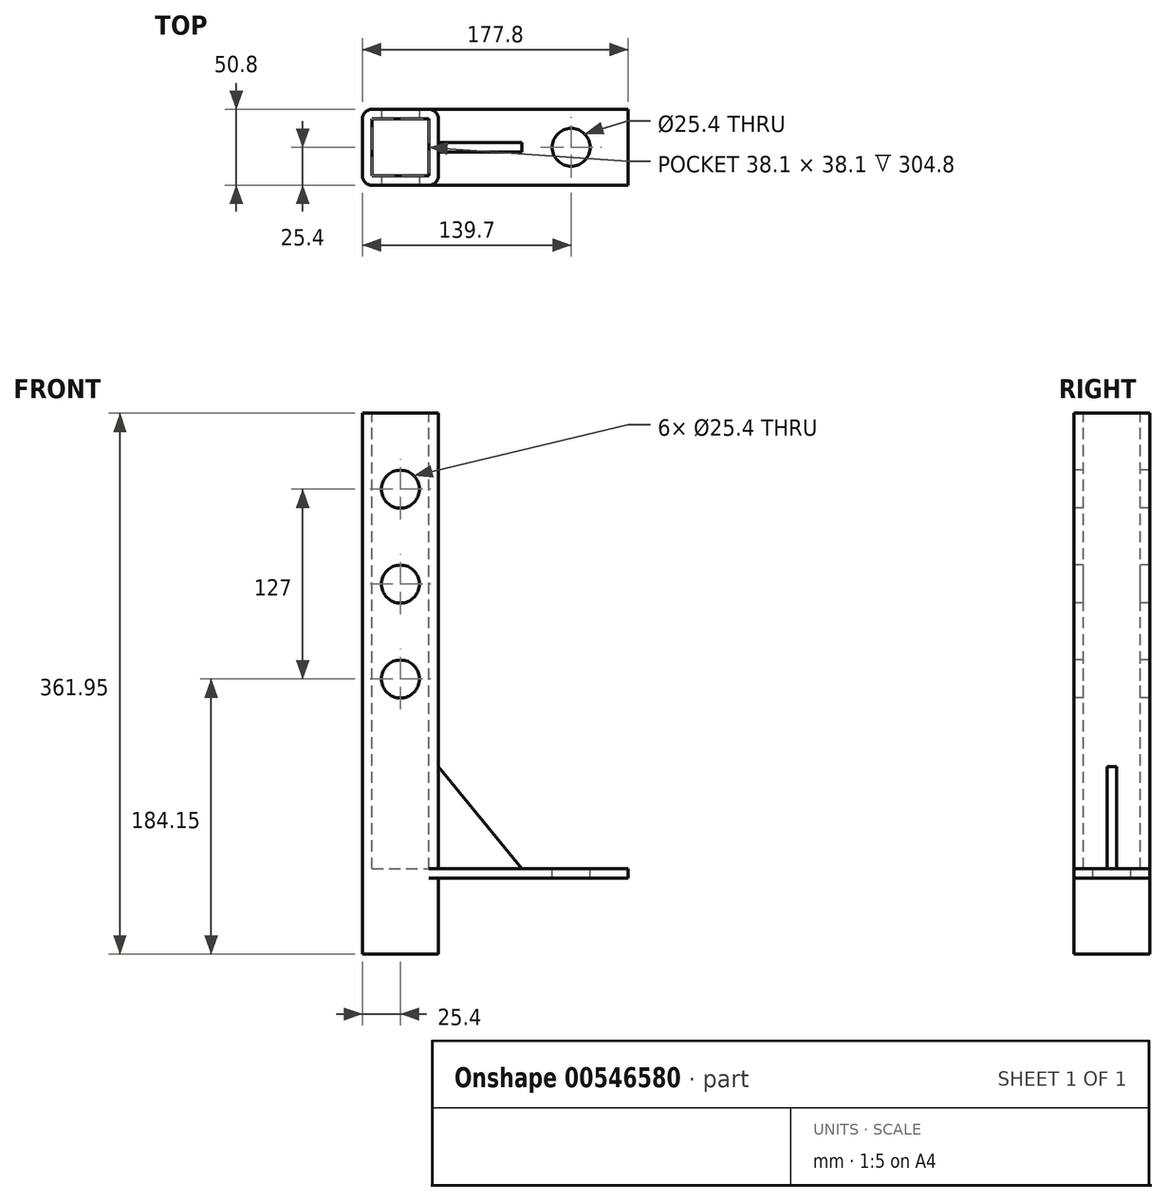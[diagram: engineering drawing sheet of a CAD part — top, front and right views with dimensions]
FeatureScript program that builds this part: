
annotation { "Feature Type Name" : "Feature", "Feature Type Description" : "" }
export const myFeature = defineFeature(function(context is Context, id is Id, definition is map)
    precondition{}
    {
        {
            var Q0;
            Q0=qCreatedBy(makeId("Top.planeOp"),FACE);
            var sketch = newSketch(context, id + "F0", { "sketchPlane" : qUnion([Q0])});
            skLineSegment(sketch, "E0.bottom", {"start": v(6.35, 0) * mm, "end": v(44.45, 0) * mm});
            skLineSegment(sketch, "E0.top", {"start": v(6.35, 50.8) * mm, "end": v(44.45, 50.8) * mm});
            skLineSegment(sketch, "E0.left", {"start": v(0, 6.35) * mm, "end": v(0, 44.45) * mm});
            skLineSegment(sketch, "E0.right", {"start": v(50.8, 6.35) * mm, "end": v(50.8, 44.45) * mm});
            skPoint(sketch, "E1.visualSharp", {"position": v(0, 50.8) * mm});
            skArc(sketch, "E1.filletArc", {"start": v(6.35, 50.8) * mm, "mid": v(1.86, 48.94) * mm, "end": v(0, 44.45) * mm});
            skPoint(sketch, "E2.visualSharp", {"position": v(50.8, 50.8) * mm});
            skArc(sketch, "E2.filletArc", {"start": v(50.8, 44.45) * mm, "mid": v(48.94, 48.94) * mm, "end": v(44.45, 50.8) * mm});
            skPoint(sketch, "E3.visualSharp", {"position": v(50.8, 0) * mm});
            skArc(sketch, "E3.filletArc", {"start": v(44.45, 0) * mm, "mid": v(48.94, 1.86) * mm, "end": v(50.8, 6.35) * mm});
            skPoint(sketch, "E4.visualSharp", {"position": v(0, 0) * mm});
            skArc(sketch, "E4.filletArc", {"start": v(0, 6.35) * mm, "mid": v(1.86, 1.86) * mm, "end": v(6.35, 0) * mm});
            skLineSegment(sketch, "E5.0", {"start": v(6.35, 44.45) * mm, "end": v(44.45, 44.45) * mm});
            skLineSegment(sketch, "E5.1", {"start": v(6.35, 6.35) * mm, "end": v(6.35, 44.45) * mm});
            skLineSegment(sketch, "E5.2", {"start": v(6.35, 6.35) * mm, "end": v(44.45, 6.35) * mm});
            skLineSegment(sketch, "E5.3", {"start": v(44.45, 6.35) * mm, "end": v(44.45, 44.45) * mm});
            skSolve(sketch);
        }
        {
            var Q0;
            Q0=makeQuery(id+"F0.imprint","IMPRINT",FACE,{"disambiguationData":[TD([[makeQuery(id+"F0.imprint","IMPRINT",EDGE,{"derivedFrom":sQuery(id+"F0.wireOp",EDGE,"E0.bottom")}),1.0]])]});
            extrude(context, id + "F1", {"entities" : qUnion([Q0]), "oppositeDirection" : true, "depth" : 304.8 * mm, "offsetDistance" : 25.4 * mm, "symmetric" : true});
        }
        {
            var Q0;
            Q0=makeQuery(id+"F1.opExtrude","SWEPT_FACE",FACE,{"disambiguationData":[OSD([sQuery(id+"F0.wireOp",EDGE,"E0.bottom")])]});
            var sketch = newSketch(context, id + "F2", { "sketchPlane" : qUnion([Q0])});
            skCircle(sketch, "E6", {"center": v(25.4, 101.6) * mm, "radius": 12.7 * mm});
            skCircle(sketch, "E7", {"center": v(25.4, 38.1) * mm, "radius": 12.7 * mm});
            skCircle(sketch, "E8", {"center": v(25.4, -25.4) * mm, "radius": 12.7 * mm});
            skLineSegment(sketch, "E9", {"start": v(25.4, 152.4) * mm, "end": v(25.4, -152.4) * mm, "construction": true});
            skSolve(sketch);
        }
        {
            var Q0;
            Q0 = qSketchRegion(id + "F2", true);
            extrude(context, id + "F3", {"entities" : qUnion([Q0]), "operationType" : NewBodyOperationType.REMOVE, "endBound" : BoundingType.THROUGH_ALL, "oppositeDirection" : true, "depth" : 25.4 * mm, "offsetDistance" : 25.4 * mm});
        }
        {
            var Q0;
            Q0=makeQuery(id+"F1.opExtrude","CAP_FACE",FACE,{"disambiguationData":[OSD([sQuery(id+"F0.wireOp",EDGE,"E0.bottom"),sQuery(id+"F0.wireOp",EDGE,"E0.top"),sQuery(id+"F0.wireOp",EDGE,"E0.left"),sQuery(id+"F0.wireOp",EDGE,"E0.right"),sQuery(id+"F0.wireOp",EDGE,"E1.filletArc"),sQuery(id+"F0.wireOp",EDGE,"E2.filletArc"),sQuery(id+"F0.wireOp",EDGE,"E3.filletArc"),sQuery(id+"F0.wireOp",EDGE,"E4.filletArc"),sQuery(id+"F0.wireOp",EDGE,"E5.0"),sQuery(id+"F0.wireOp",EDGE,"E5.1"),sQuery(id+"F0.wireOp",EDGE,"E5.2"),sQuery(id+"F0.wireOp",EDGE,"E5.3")])],"isStart":false});
            var sketch = newSketch(context, id + "F4", { "sketchPlane" : qUnion([Q0])});
            skLineSegment(sketch, "E10.0", {"start": v(0, -6.35) * mm, "end": v(0, -44.45) * mm});
            skArc(sketch, "E11.0", {"start": v(6.35, -50.8) * mm, "mid": v(1.86, -48.94) * mm, "end": v(0, -44.45) * mm});
            skLineSegment(sketch, "E12.0", {"start": v(6.35, -50.8) * mm, "end": v(44.45, -50.8) * mm});
            skLineSegment(sketch, "E13.0", {"start": v(50.8, -6.35) * mm, "end": v(50.8, -44.45) * mm});
            skArc(sketch, "E14.0", {"start": v(50.8, -44.45) * mm, "mid": v(48.94, -48.94) * mm, "end": v(44.45, -50.8) * mm});
            skArc(sketch, "E15.0", {"start": v(44.45, 0) * mm, "mid": v(48.94, -1.86) * mm, "end": v(50.8, -6.35) * mm});
            skLineSegment(sketch, "E16.0", {"start": v(6.35, 0) * mm, "end": v(44.45, 0) * mm});
            skArc(sketch, "E17.0", {"start": v(0, -6.35) * mm, "mid": v(1.86, -1.86) * mm, "end": v(6.35, 0) * mm});
            skPoint(sketch, "E18.0", {"position": v(0, 0) * mm});
            skLineSegment(sketch, "E19.bottom", {"start": v(6.35, 0) * mm, "end": v(177.8, 0) * mm});
            skLineSegment(sketch, "E19.top", {"start": v(6.35, -50.8) * mm, "end": v(177.8, -50.8) * mm});
            skLineSegment(sketch, "E19.right", {"start": v(177.8, 0) * mm, "end": v(177.8, -50.8) * mm});
            skArc(sketch, "E20.filletArc", {"start": v(6.35, 0) * mm, "mid": v(1.86, -1.86) * mm, "end": v(0, -6.35) * mm});
            skPoint(sketch, "E21.visualSharp", {"position": v(0, -50.8) * mm});
            skArc(sketch, "E21.filletArc", {"start": v(0, -44.45) * mm, "mid": v(1.86, -48.94) * mm, "end": v(6.35, -50.8) * mm});
            skSolve(sketch);
        }
        {
            var Q0;
            Q0 = qSketchRegion(id + "F4", true);
            extrude(context, id + "F5", {"entities" : qUnion([Q0]), "operationType" : NewBodyOperationType.ADD, "depth" : 6.35 * mm, "offsetDistance" : 25.4 * mm});
        }
        {
            var Q0;
            {var subQ0=sQuery(id+"F4.wireOp",EDGE,"E19.bottom");var subQ1=sQuery(id+"F4.wireOp",EDGE,"E19.top");var subQ2=sQuery(id+"F4.wireOp",EDGE,"E19.right");Q0=makeQuery(id+"F5.boolean.opBoolean","SPLIT",FACE,{"disambiguationData":[TD([makeQuery(id+"F1.opExtrude","SWEPT_FACE",FACE,{"disambiguationData":[OSD([sQuery(id+"F0.wireOp",EDGE,"E0.bottom")])]})])],"derivedFrom":makeQuery(id+"F5.opExtrude","CAP_FACE",FACE,{"disambiguationData":[OSD([subQ0,subQ1,sQuery(id+"F4.wireOp",EDGE,"E10.0"),subQ2,sQuery(id+"F4.wireOp",EDGE,"E20.filletArc"),sQuery(id+"F4.wireOp",EDGE,"E21.filletArc")])],"isStart":true})});}
            var sketch = newSketch(context, id + "F6", { "sketchPlane" : qUnion([Q0])});
            skCircle(sketch, "E22", {"center": v(139.7, 25.4) * mm, "radius": 12.7 * mm});
            skLineSegment(sketch, "E23", {"start": v(177.8, 25.4) * mm, "end": v(50.8, 25.4) * mm, "construction": true});
            skSolve(sketch);
        }
        {
            var Q0;
            Q0 = qSketchRegion(id + "F6", true);
            extrude(context, id + "F7", {"entities" : qUnion([Q0]), "operationType" : NewBodyOperationType.REMOVE, "endBound" : BoundingType.THROUGH_ALL, "oppositeDirection" : true, "depth" : 25.4 * mm, "offsetDistance" : 25.4 * mm});
        }
        {
            var Q0;
            Q0=makeQuery(id+"F5.boolean.opBoolean","MERGE",FACE,{"derivedFrom":[makeQuery(id+"F1.opExtrude","SWEPT_FACE",FACE,{"disambiguationData":[OSD([sQuery(id+"F0.wireOp",EDGE,"E0.bottom")])]}),makeQuery(id+"F5.opExtrude","SWEPT_FACE",FACE,{"disambiguationData":[OSD([sQuery(id+"F4.wireOp",EDGE,"E19.bottom")])]})]});
            cPlane(context, id + "F8", {"entities" : qUnion([Q0]), "cplaneType" : CPlaneType.OFFSET, "offset" : 25.4 * mm, "oppositeDirection" : true, "width" : 152.4 * mm, "height" : 152.4 * mm});
        }
        {
            var Q0;
            Q0=qCreatedBy(id+"F8.planeOp",FACE);
            var sketch = newSketch(context, id + "F9", { "sketchPlane" : qUnion([Q0])});
            skLineSegment(sketch, "E24.0", {"start": v(50.8, -152.4) * mm, "end": v(50.8, 152.4) * mm});
            skLineSegment(sketch, "E25.0", {"start": v(44.45, -152.4) * mm, "end": v(177.8, -152.4) * mm});
            skLineSegment(sketch, "E26.bottom", {"start": v(50.8, -152.4) * mm, "end": v(106.74, -152.4) * mm});
            skLineSegment(sketch, "E26.left", {"start": v(50.8, -152.4) * mm, "end": v(50.8, -83.86) * mm});
            skLineSegment(sketch, "E27", {"start": v(50.8, -83.86) * mm, "end": v(106.74, -152.4) * mm});
            skSolve(sketch);
        }
        {
            var Q0;
            Q0 = qSketchRegion(id + "F9", true);
            extrude(context, id + "F10", {"entities" : qUnion([Q0]), "operationType" : NewBodyOperationType.ADD, "depth" : 6.35 * mm, "offsetDistance" : 25.4 * mm, "symmetric" : true});
        }
        {
            var Q0;
            Q0=makeQuery(id+"F5.opExtrude","CAP_FACE",FACE,{"disambiguationData":[OSD([sQuery(id+"F4.wireOp",EDGE,"E19.bottom"),sQuery(id+"F4.wireOp",EDGE,"E19.top"),sQuery(id+"F4.wireOp",EDGE,"E10.0"),sQuery(id+"F4.wireOp",EDGE,"E19.right"),sQuery(id+"F4.wireOp",EDGE,"E20.filletArc"),sQuery(id+"F4.wireOp",EDGE,"E21.filletArc")])],"isStart":false});
            var sketch = newSketch(context, id + "F11", { "sketchPlane" : qUnion([Q0])});
            skLineSegment(sketch, "E28.0", {"start": v(0, -6.35) * mm, "end": v(0, -44.45) * mm});
            skArc(sketch, "E29.0", {"start": v(0, -6.35) * mm, "mid": v(1.86, -1.86) * mm, "end": v(6.35, 0) * mm});
            skLineSegment(sketch, "E30.0", {"start": v(6.35, 0) * mm, "end": v(177.8, 0) * mm});
            skArc(sketch, "E31.0", {"start": v(6.35, -50.8) * mm, "mid": v(1.86, -48.94) * mm, "end": v(0, -44.45) * mm});
            skLineSegment(sketch, "E32.0", {"start": v(6.35, -50.8) * mm, "end": v(177.8, -50.8) * mm});
            skArc(sketch, "E33.0.0", {"start": v(50.8, -6.35) * mm, "mid": v(48.94, -1.86) * mm, "end": v(44.45, 0) * mm});
            skArc(sketch, "E33.0.2", {"start": v(44.45, 0) * mm, "mid": v(48.94, -1.86) * mm, "end": v(50.8, -6.35) * mm});
            skLineSegment(sketch, "E34", {"start": v(0, -44.45) * mm, "end": v(0, -6.35) * mm});
            skArc(sketch, "E35", {"start": v(6.35, 0) * mm, "mid": v(1.86, -1.86) * mm, "end": v(0, -6.35) * mm});
            skLineSegment(sketch, "E36", {"start": v(6.35, 0) * mm, "end": v(44.45, 0) * mm});
            skArc(sketch, "E37", {"start": v(0, -44.45) * mm, "mid": v(1.86, -48.94) * mm, "end": v(6.35, -50.8) * mm});
            skArc(sketch, "E38.0.0", {"start": v(44.45, -50.8) * mm, "mid": v(48.94, -48.94) * mm, "end": v(50.8, -44.45) * mm});
            skArc(sketch, "E38.0.2", {"start": v(50.8, -44.45) * mm, "mid": v(48.94, -48.94) * mm, "end": v(44.45, -50.8) * mm});
            skLineSegment(sketch, "E39", {"start": v(50.8, -6.35) * mm, "end": v(50.8, -44.45) * mm});
            skLineSegment(sketch, "E40", {"start": v(6.35, -50.8) * mm, "end": v(44.45, -50.8) * mm});
            skSolve(sketch);
        }
        {
            var Q0;
            Q0 = qSketchRegion(id + "F11", true);
            extrude(context, id + "F12", {"entities" : qUnion([Q0]), "operationType" : NewBodyOperationType.ADD, "depth" : 50.8 * mm, "offsetDistance" : 25.4 * mm});
        }
    });
